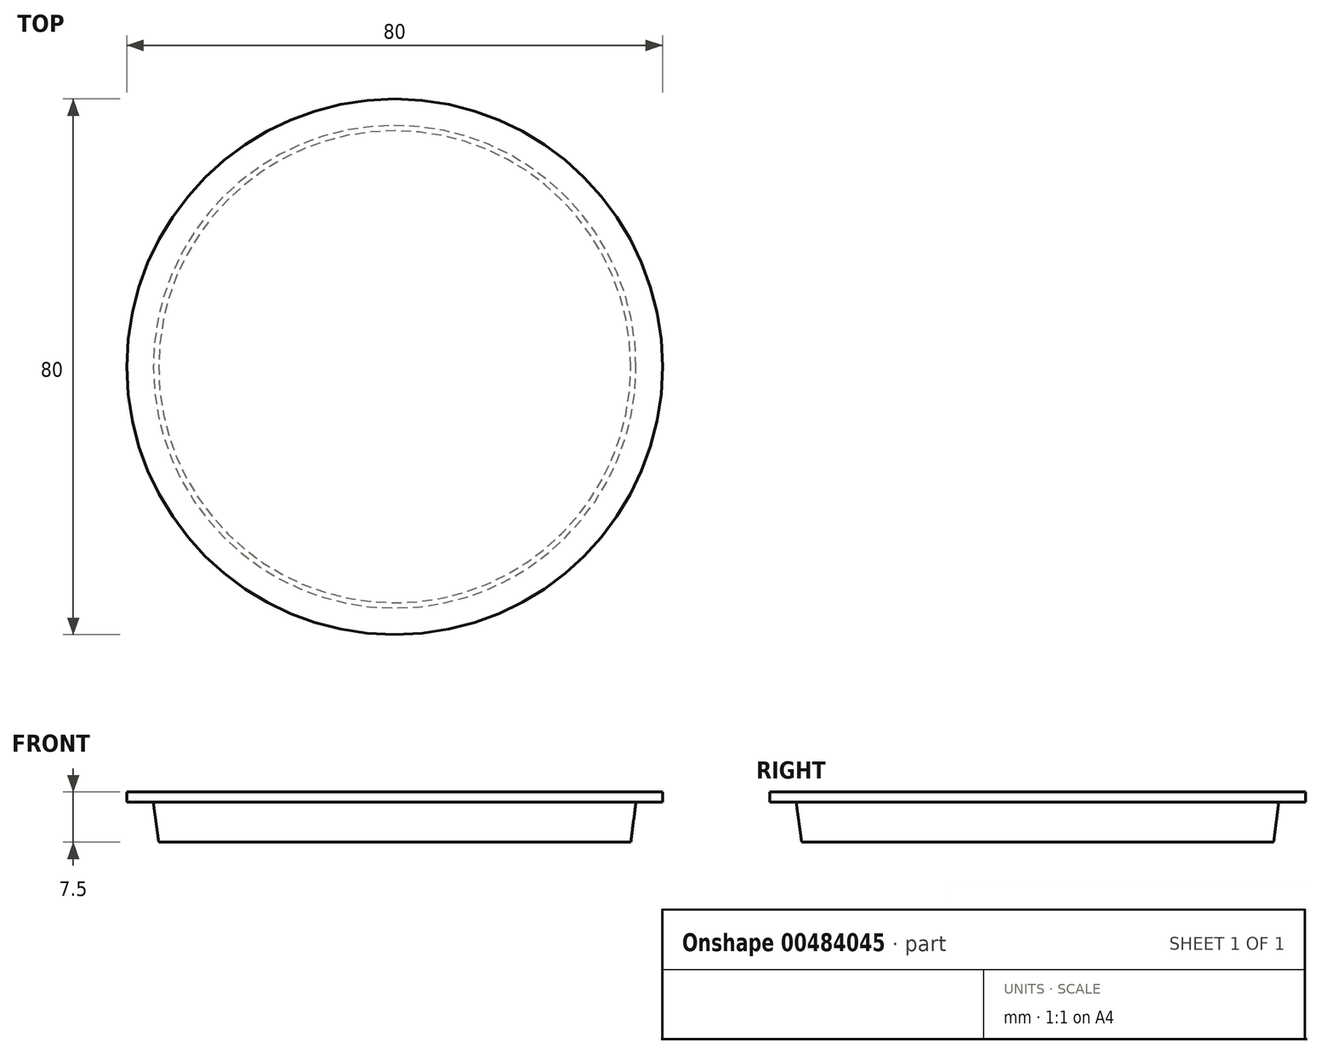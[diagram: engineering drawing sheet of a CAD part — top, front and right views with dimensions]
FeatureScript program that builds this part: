
annotation { "Feature Type Name" : "Feature", "Feature Type Description" : "" }
export const myFeature = defineFeature(function(context is Context, id is Id, definition is map)
    precondition{}
    {
        {
            var Q0;
            Q0=qCreatedBy(makeId("Top.planeOp"),FACE);
            var sketch = newSketch(context, id + "F0", { "sketchPlane" : qUnion([Q0])});
            skCircle(sketch, "E0", {"center": v(0, 0) * mm, "radius": 35.25 * mm});
            skSolve(sketch);
        }
        {
            var Q0;
            Q0=makeQuery(id+"F0.imprint","IMPRINT",FACE,{"disambiguationData":[TD([[makeQuery(id+"F0.imprint","IMPRINT",EDGE,{"derivedFrom":sQuery(id+"F0.wireOp",EDGE,"E0")}),1.0]])]});
            extrude(context, id + "F1", {"entities" : qUnion([Q0]), "depth" : 6 * mm, "hasDraft" : true, "draftAngle" : 7.5 * degree});
        }
        {
            var Q0;
            Q0=makeQuery(id+"F1.opExtrude","CAP_FACE",FACE,{"disambiguationData":[OSD([sQuery(id+"F0.wireOp",EDGE,"E0")])],"isStart":false});
            var sketch = newSketch(context, id + "F2", { "sketchPlane" : qUnion([Q0])});
            skCircle(sketch, "E1", {"center": v(0, 0) * mm, "radius": 40 * mm});
            skSolve(sketch);
        }
        {
            var Q0;
            Q0=makeQuery(id+"F2.imprint","IMPRINT",FACE,{"disambiguationData":[TD([[makeQuery(id+"F2.imprint","IMPRINT",EDGE,{"derivedFrom":sQuery(id+"F2.wireOp",EDGE,"E1")}),1.0]])]});
            var Q1;
            Q1=makeQuery(id+"F2.imprint","IMPRINT",FACE,{"disambiguationData":[TD([[makeQuery(id+"F2.imprint","IMPRINT",EDGE,{"derivedFrom":makeQuery(id+"F1.opExtrude","CAP_EDGE",EDGE,{"disambiguationData":[OSD([sQuery(id+"F0.wireOp",EDGE,"E0")])],"isStart":false})}),1.0]])]});
            var Q2;
            Q2=sQuery(id+"F2.wireOp",EDGE,"E1");
            extrude(context, id + "F3", {"entities" : qUnion([Q0, Q1]), "operationType" : NewBodyOperationType.ADD, "surfaceEntities" : qUnion([Q2]), "depth" : 1.5 * mm});
        }
    });
